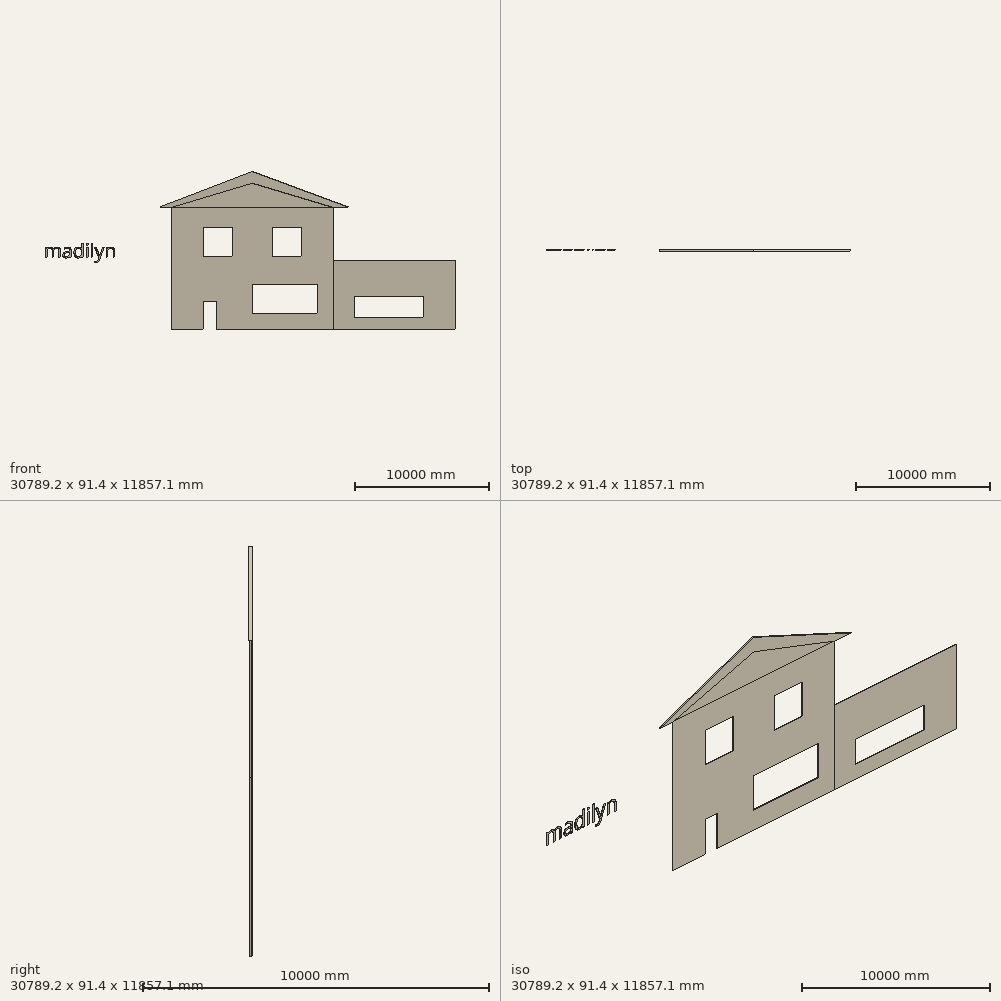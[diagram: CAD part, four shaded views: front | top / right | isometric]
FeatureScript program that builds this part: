
annotation { "Feature Type Name" : "Feature", "Feature Type Description" : "" }
export const myFeature = defineFeature(function(context is Context, id is Id, definition is map)
    precondition{}
    {
        {
            var Q0;
            Q0=qCreatedBy(makeId("Front.planeOp"),FACE);
            var sketch = newSketch(context, id + "F0", { "sketchPlane" : qUnion([Q0])});
            skLineSegment(sketch, "E0", {"start": v(0, 0) * mm, "end": v(6096, 0) * mm});
            skLineSegment(sketch, "E1", {"start": v(-6096, 0) * mm, "end": v(-6096, -9144) * mm});
            skLineSegment(sketch, "E2", {"start": v(6096, 0) * mm, "end": v(6096, -9144) * mm});
            skLineSegment(sketch, "E3", {"start": v(-6096, -9144) * mm, "end": v(6096, -9144) * mm});
            skLineSegment(sketch, "E4", {"start": v(0, 0) * mm, "end": v(0, 914.4) * mm});
            skLineSegment(sketch, "E5", {"start": v(0, 914.4) * mm, "end": v(0, 1828.8) * mm});
            skLineSegment(sketch, "E6", {"start": v(0, 1828.8) * mm, "end": v(6096, 0) * mm});
            skLineSegment(sketch, "E7", {"start": v(0, 1828.8) * mm, "end": v(-6096, 0) * mm});
            skLineSegment(sketch, "E8", {"start": v(-6096, 0) * mm, "end": v(-7072.34, 0) * mm});
            skLineSegment(sketch, "E9", {"start": v(0, 2713.11) * mm, "end": v(-7072.34, 0) * mm});
            skLineSegment(sketch, "E10", {"start": v(6096, 0) * mm, "end": v(7314.25, 0) * mm});
            skLineSegment(sketch, "E11", {"start": v(7314.25, 0) * mm, "end": v(0, 2713.11) * mm});
            skPoint(sketch, "E12.endSnap0", {"position": v(0, -9144) * mm});
            skLineSegment(sketch, "E13", {"start": v(4876.8, -5791.2) * mm, "end": v(0, -5791.2) * mm});
            skLineSegment(sketch, "E14", {"start": v(0, -5791.2) * mm, "end": v(0, -7924.8) * mm});
            skLineSegment(sketch, "E15", {"start": v(4876.8, -5791.2) * mm, "end": v(4876.8, -7924.8) * mm});
            skLineSegment(sketch, "E16", {"start": v(0, -7924.8) * mm, "end": v(4876.8, -7924.8) * mm});
            skPoint(sketch, "E17.endSnap0", {"position": v(6096, -4572) * mm});
            skLineSegment(sketch, "E18", {"start": v(6096, -9144) * mm, "end": v(15240, -9144) * mm});
            skLineSegment(sketch, "E19", {"start": v(7620, -6705.6) * mm, "end": v(12801.6, -6705.6) * mm});
            skLineSegment(sketch, "E20", {"start": v(7620, -6705.6) * mm, "end": v(7620, -8229.6) * mm});
            skLineSegment(sketch, "E21", {"start": v(12801.6, -6705.6) * mm, "end": v(12801.6, -8229.6) * mm});
            skText(sketch, "E22", { "text": "madilyn\n", "fontName": "OpenSans-Regular.ttf"});
            skLineSegment(sketch, "E23", {"start": v(15240, -5181.6) * mm, "end": v(6096, -5181.6) * mm});
            skLineSegment(sketch, "E24", {"start": v(15240, -9144) * mm, "end": v(15240, -3962.4) * mm});
            skLineSegment(sketch, "E25", {"start": v(15240, -3962.4) * mm, "end": v(6096, -3962.4) * mm});
            skLineSegment(sketch, "E26", {"start": v(7620, -8229.6) * mm, "end": v(12801.6, -8229.6) * mm});
            skLineSegment(sketch, "E27", {"start": v(-6096, 0) * mm, "end": v(0, 0) * mm});
            skLineSegment(sketch, "E28.bottom", {"start": v(-3657.6, -7010.4) * mm, "end": v(-2743.2, -7010.4) * mm});
            skLineSegment(sketch, "E28.top", {"start": v(-3657.6, -9144) * mm, "end": v(-2743.2, -9144) * mm});
            skLineSegment(sketch, "E28.left", {"start": v(-3657.6, -7010.4) * mm, "end": v(-3657.6, -9144) * mm});
            skLineSegment(sketch, "E28.right", {"start": v(-2743.2, -7010.4) * mm, "end": v(-2743.2, -9144) * mm});
            skLineSegment(sketch, "E29.bottom", {"start": v(-3657.6, -1524) * mm, "end": v(-1524, -1524) * mm});
            skLineSegment(sketch, "E29.top", {"start": v(-3657.6, -3657.6) * mm, "end": v(-1524, -3657.6) * mm});
            skLineSegment(sketch, "E29.left", {"start": v(-3657.6, -1524) * mm, "end": v(-3657.6, -3657.6) * mm});
            skLineSegment(sketch, "E29.right", {"start": v(-1524, -1524) * mm, "end": v(-1524, -3657.6) * mm});
            skLineSegment(sketch, "E30.bottom", {"start": v(1524, -1524) * mm, "end": v(3657.6, -1524) * mm});
            skLineSegment(sketch, "E30.top", {"start": v(1524, -3657.6) * mm, "end": v(3657.6, -3657.6) * mm});
            skLineSegment(sketch, "E30.left", {"start": v(1524, -1524) * mm, "end": v(1524, -3657.6) * mm});
            skLineSegment(sketch, "E30.right", {"start": v(3657.6, -1524) * mm, "end": v(3657.6, -3657.6) * mm});
            const initialGuessF0  = {"E22": [-15.67508, -3.7686, 1, 0, 1.05503]};
            skSetInitialGuess(sketch, initialGuessF0);
            skSolve(sketch);
        }
        {
            var Q0;
            Q0=makeQuery(id+"F0.imprint","IMPRINT",FACE,{"disambiguationData":[TD([[makeQuery(id+"F0.imprint","IMPRINT",EDGE,{"derivedFrom":sQuery(id+"F0.wireOp",EDGE,"E22.sketch_text.stroke-0")}),-1.0]])]});
            var Q1;
            Q1=makeQuery(id+"F0.imprint","IMPRINT",FACE,{"disambiguationData":[TD([[makeQuery(id+"F0.imprint","IMPRINT",EDGE,{"derivedFrom":sQuery(id+"F0.wireOp",EDGE,"E22.sketch_text.stroke-79")}),-1.0]])]});
            var Q2;
            Q2=makeQuery(id+"F0.imprint","IMPRINT",FACE,{"disambiguationData":[TD([[makeQuery(id+"F0.imprint","IMPRINT",EDGE,{"derivedFrom":sQuery(id+"F0.wireOp",EDGE,"E22.sketch_text.stroke-83")}),-1.0]])]});
            var Q3;
            Q3=makeQuery(id+"F0.imprint","IMPRINT",FACE,{"disambiguationData":[TD([[makeQuery(id+"F0.imprint","IMPRINT",EDGE,{"derivedFrom":sQuery(id+"F0.wireOp",EDGE,"E22.sketch_text.stroke-91")}),-1.0]])]});
            var Q4;
            Q4=makeQuery(id+"F0.imprint","IMPRINT",FACE,{"disambiguationData":[TD([[makeQuery(id+"F0.imprint","IMPRINT",EDGE,{"derivedFrom":sQuery(id+"F0.wireOp",EDGE,"E22.sketch_text.stroke-95")}),-1.0]])]});
            var Q5;
            Q5=makeQuery(id+"F0.imprint","IMPRINT",FACE,{"disambiguationData":[TD([[makeQuery(id+"F0.imprint","IMPRINT",EDGE,{"derivedFrom":sQuery(id+"F0.wireOp",EDGE,"E22.sketch_text.stroke-111")}),-1.0]])]});
            var Q6;
            Q6=makeQuery(id+"F0.imprint","IMPRINT",FACE,{"disambiguationData":[TD([[makeQuery(id+"F0.imprint","IMPRINT",EDGE,{"derivedFrom":sQuery(id+"F0.wireOp",EDGE,"E22.sketch_text.stroke-28")}),-1.0]])]});
            var Q7;
            Q7=makeQuery(id+"F0.imprint","IMPRINT",FACE,{"disambiguationData":[TD([[makeQuery(id+"F0.imprint","IMPRINT",EDGE,{"derivedFrom":sQuery(id+"F0.wireOp",EDGE,"E22.sketch_text.stroke-55")}),-1.0]])]});
            var Q8;
            Q8=makeQuery(id+"F0.imprint","IMPRINT",FACE,{"disambiguationData":[TD([[makeQuery(id+"F0.imprint","IMPRINT",EDGE,{"derivedFrom":sQuery(id+"F0.wireOp",EDGE,"E0")}),1.0]])]});
            var Q9;
            Q9=makeQuery(id+"F0.imprint","IMPRINT",FACE,{"disambiguationData":[TD([[makeQuery(id+"F0.imprint","IMPRINT",EDGE,{"derivedFrom":sQuery(id+"F0.wireOp",EDGE,"E4")}),1.0]])]});
            var Q10;
            Q10=makeQuery(id+"F0.imprint","IMPRINT",FACE,{"disambiguationData":[TD([[makeQuery(id+"F0.imprint","IMPRINT",EDGE,{"derivedFrom":sQuery(id+"F0.wireOp",EDGE,"E6")}),1.0]])]});
            var Q11;
            {var subQ5=sQuery(id+"F0.wireOp",EDGE,"E0");Q11=makeQuery(id+"F0.imprint","IMPRINT",FACE,{"disambiguationData":[TD([[makeQuery(id+"F0.imprint","IMPRINT",EDGE,{"derivedFrom":subQ5}),-1.0]])]});}
            extrude(context, id + "F1", {"entities" : qUnion([Q0, Q1, Q2, Q3, Q4, Q5, Q6, Q7, Q8, Q9, Q10, Q11]), "oppositeDirection" : true, "depth" : 30.48 * mm, "offsetDistance" : 30.48 * mm});
        }
        {
            var Q0;
            Q0=makeQuery(id+"F0.imprint","IMPRINT",FACE,{"disambiguationData":[TD([[makeQuery(id+"F0.imprint","IMPRINT",EDGE,{"derivedFrom":sQuery(id+"F0.wireOp",EDGE,"E6")}),1.0]])]});
            var Q1;
            {var subQ1=sQuery(id+"F0.wireOp",EDGE,"E18");Q1=makeQuery(id+"F0.imprint","IMPRINT",FACE,{"disambiguationData":[TD([[makeQuery(id+"F0.imprint","IMPRINT",EDGE,{"derivedFrom":subQ1}),1.0]])]});}
            var Q2;
            {var subQ0=sQuery(id+"F0.wireOp",EDGE,"E23");Q2=makeQuery(id+"F0.imprint","IMPRINT",FACE,{"disambiguationData":[TD([[makeQuery(id+"F0.imprint","IMPRINT",EDGE,{"derivedFrom":subQ0}),-1.0]])]});}
            extrude(context, id + "F2", {"entities" : qUnion([Q0, Q1, Q2]), "operationType" : NewBodyOperationType.ADD, "depth" : 30.48 * mm, "offsetDistance" : 30.48 * mm});
        }
        {
            var Q0;
            Q0=makeQuery(id+"F2.opExtrude","CAP_FACE",FACE,{"disambiguationData":[OSD([sQuery(id+"F0.wireOp",EDGE,"E6"),sQuery(id+"F0.wireOp",EDGE,"E7"),sQuery(id+"F0.wireOp",EDGE,"E8"),sQuery(id+"F0.wireOp",EDGE,"E9"),sQuery(id+"F0.wireOp",EDGE,"E10"),sQuery(id+"F0.wireOp",EDGE,"E11")])],"isStart":false});
            extrude(context, id + "F3", {"entities" : qUnion([Q0]), "operationType" : NewBodyOperationType.ADD, "depth" : 30.48 * mm, "offsetDistance" : 30.48 * mm});
        }
        {
            var Q0;
            Q0=makeQuery(id+"F0.imprint","IMPRINT",FACE,{"disambiguationData":[TD([[makeQuery(id+"F0.imprint","IMPRINT",EDGE,{"derivedFrom":sQuery(id+"F0.wireOp",EDGE,"E4")}),1.0]])]});
            var Q1;
            Q1=makeQuery(id+"F0.imprint","IMPRINT",FACE,{"disambiguationData":[TD([[makeQuery(id+"F0.imprint","IMPRINT",EDGE,{"derivedFrom":sQuery(id+"F0.wireOp",EDGE,"E0")}),1.0]])]});
            extrude(context, id + "F4", {"entities" : qUnion([Q0, Q1]), "operationType" : NewBodyOperationType.ADD, "depth" : 30.48 * mm, "offsetDistance" : 30.48 * mm});
        }
        {
            var Q0;
            {var subQ5=sQuery(id+"F0.wireOp",EDGE,"E0");Q0=makeQuery(id+"F0.imprint","IMPRINT",FACE,{"disambiguationData":[TD([[makeQuery(id+"F0.imprint","IMPRINT",EDGE,{"derivedFrom":subQ5}),-1.0]])]});}
            extrude(context, id + "F5", {"entities" : qUnion([Q0]), "depth" : 30.48 * mm, "offsetDistance" : 30.48 * mm});
        }
    });
